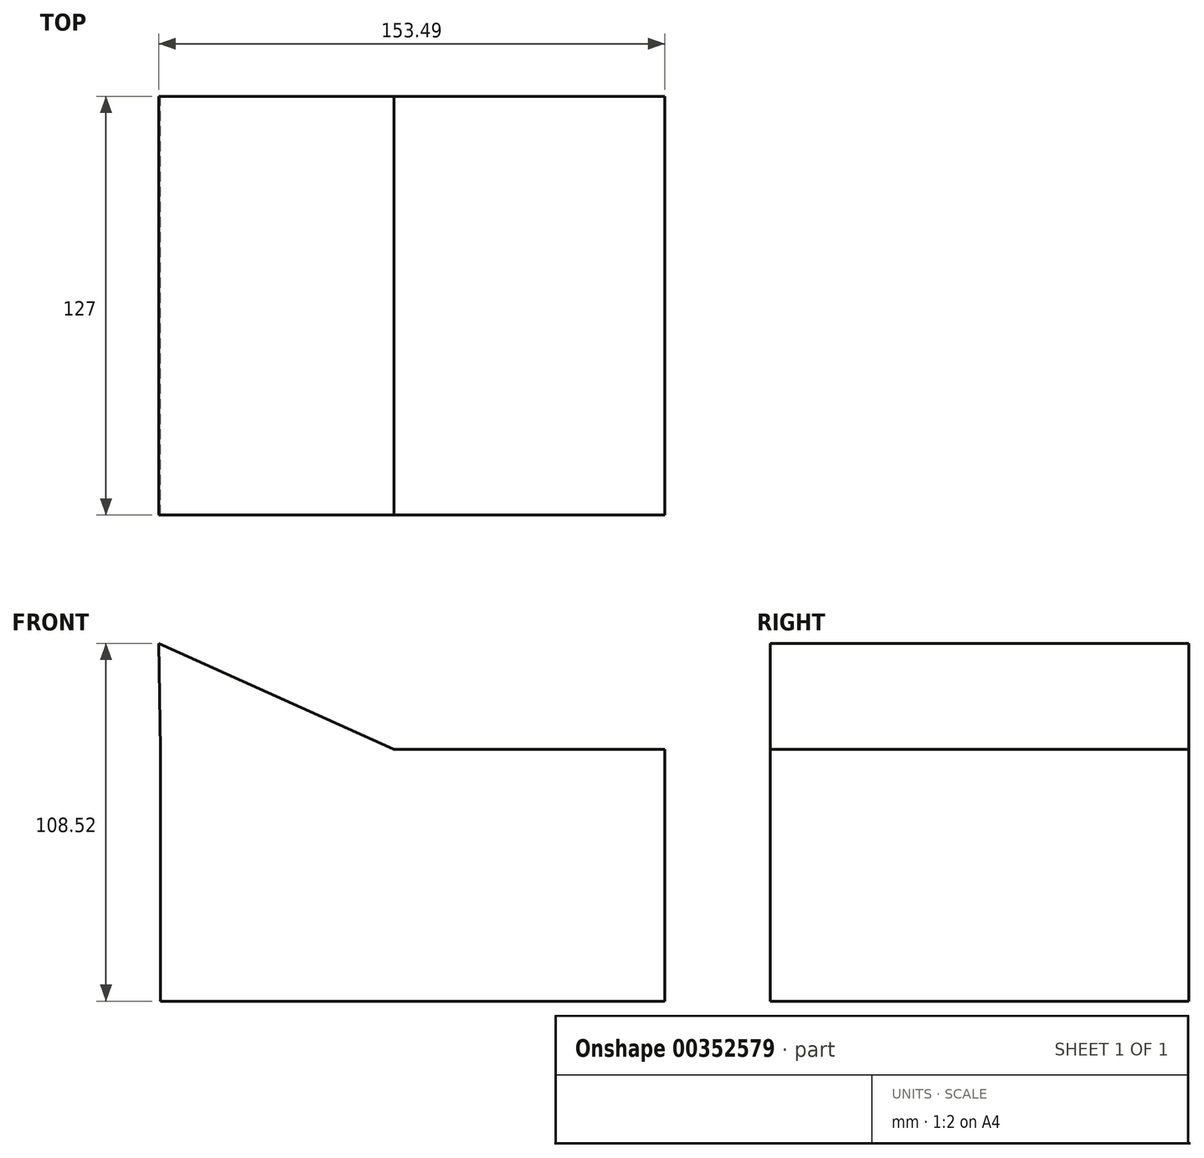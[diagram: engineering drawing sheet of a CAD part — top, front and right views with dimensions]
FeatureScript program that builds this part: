
annotation { "Feature Type Name" : "Feature", "Feature Type Description" : "" }
export const myFeature = defineFeature(function(context is Context, id is Id, definition is map)
    precondition{}
    {
        {
            var Q0;
            Q0=qCreatedBy(makeId("Front.planeOp"),FACE);
            var sketch = newSketch(context, id + "F0", { "sketchPlane" : qUnion([Q0])});
            skLineSegment(sketch, "E0", {"start": v(-64.56, 45.6) * mm, "end": v(-64.56, -30.77) * mm});
            skLineSegment(sketch, "E1", {"start": v(-64.56, -30.77) * mm, "end": v(88.43, -30.77) * mm});
            skLineSegment(sketch, "E2", {"start": v(88.43, -30.77) * mm, "end": v(88.43, 45.6) * mm});
            skLineSegment(sketch, "E3", {"start": v(88.43, 45.6) * mm, "end": v(6.28, 45.6) * mm});
            skLineSegment(sketch, "E4", {"start": v(6.28, 45.6) * mm, "end": v(-65.06, 77.75) * mm});
            skLineSegment(sketch, "E5", {"start": v(-65.06, 77.75) * mm, "end": v(-64.56, 45.6) * mm});
            skSolve(sketch);
        }
        {
            var Q0;
            Q0=makeQuery(id+"F0.imprint","IMPRINT",FACE,{"disambiguationData":[TD([[makeQuery(id+"F0.imprint","IMPRINT",EDGE,{"derivedFrom":sQuery(id+"F0.wireOp",EDGE,"E0")}),1.0]])]});
            extrude(context, id + "F1", {"entities" : qUnion([Q0]), "depth" : 127 * mm});
        }
    });
